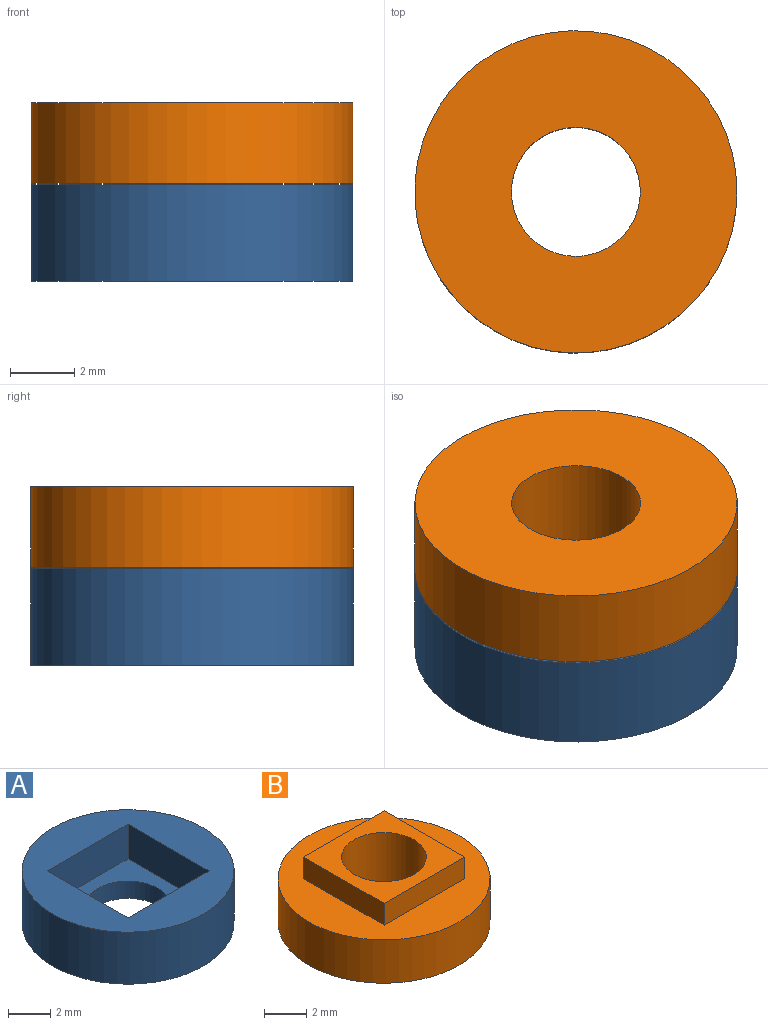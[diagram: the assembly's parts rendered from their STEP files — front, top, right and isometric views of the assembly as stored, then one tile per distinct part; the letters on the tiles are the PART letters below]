
ASSEMBLY  parts=2 mates=1
PART A: 9 faces, bbox 10x10x3 mm
  f0: cylinder r=2mm len=4mm, axis (0,0,-1), area 12.6mm2, adj f1,f2
  f1: plane 5.4x5.4mm, normal (0,0,1), area 16.6mm2, adj f0,f3,f4,f5,f6
  f2: plane 10x10mm, normal (0,0,-1), area 66mm2, adj f0,f7
  f3: plane 5.4x2mm, normal (1,0,0), area 10.8mm2, adj f1,f4,f6,f8
  f4: plane 5.4x2mm, normal (0,1,0), area 10.8mm2, adj f1,f3,f5,f8
  f5: plane 5.4x2mm, normal (-1,0,0), area 10.8mm2, adj f1,f4,f6,f8
  f6: plane 5.4x2mm, normal (0,-1,0), area 10.8mm2, adj f1,f3,f5,f8
  f7: cylinder r=5mm len=10mm, axis (0,0,-1), area 94.2mm2, adj f2,f8
  f8: plane 10x10mm, normal (0,0,1), area 49.4mm2, adj f3,f4,f5,f6,f7
PART B: 9 faces, bbox 10x10x3.8 mm
  f0: cylinder r=5mm len=10mm, axis (0,0,-1), area 78.5mm2, adj f1,f2
  f1: plane 10x10mm, normal (0,0,1), area 49.9mm2, adj f0,f3,f4,f5,f6
  f2: plane 10x10mm, normal (0,0,-1), area 66mm2, adj f0,f7
  f3: plane 5.35x1.25mm, normal (-1,0,0), area 6.7mm2, adj f1,f4,f6,f8
  f4: plane 5.35x1.25mm, normal (0,-1,0), area 6.7mm2, adj f1,f3,f5,f8
  f5: plane 5.35x1.25mm, normal (1,0,0), area 6.7mm2, adj f1,f4,f6,f8
  f6: plane 5.35x1.25mm, normal (0,1,0), area 6.7mm2, adj f1,f3,f5,f8
  f7: cylinder r=2mm len=4mm, axis (0,0,-1), area 47.1mm2, adj f2,f8
  f8: plane 5.35x5.35mm, normal (0,0,1), area 16.1mm2, adj f3,f4,f5,f6,f7
PLACE A t=(-0.27,-3.84,0)mm
PLACE B rot(axis=(1,0,0),180deg) t=(-0.27,-3.84,5.55)mm
MATE slider B.f7 <-> A.f0  axis (0,0,-1) through (-0.27,-3.84,1.8)mm
